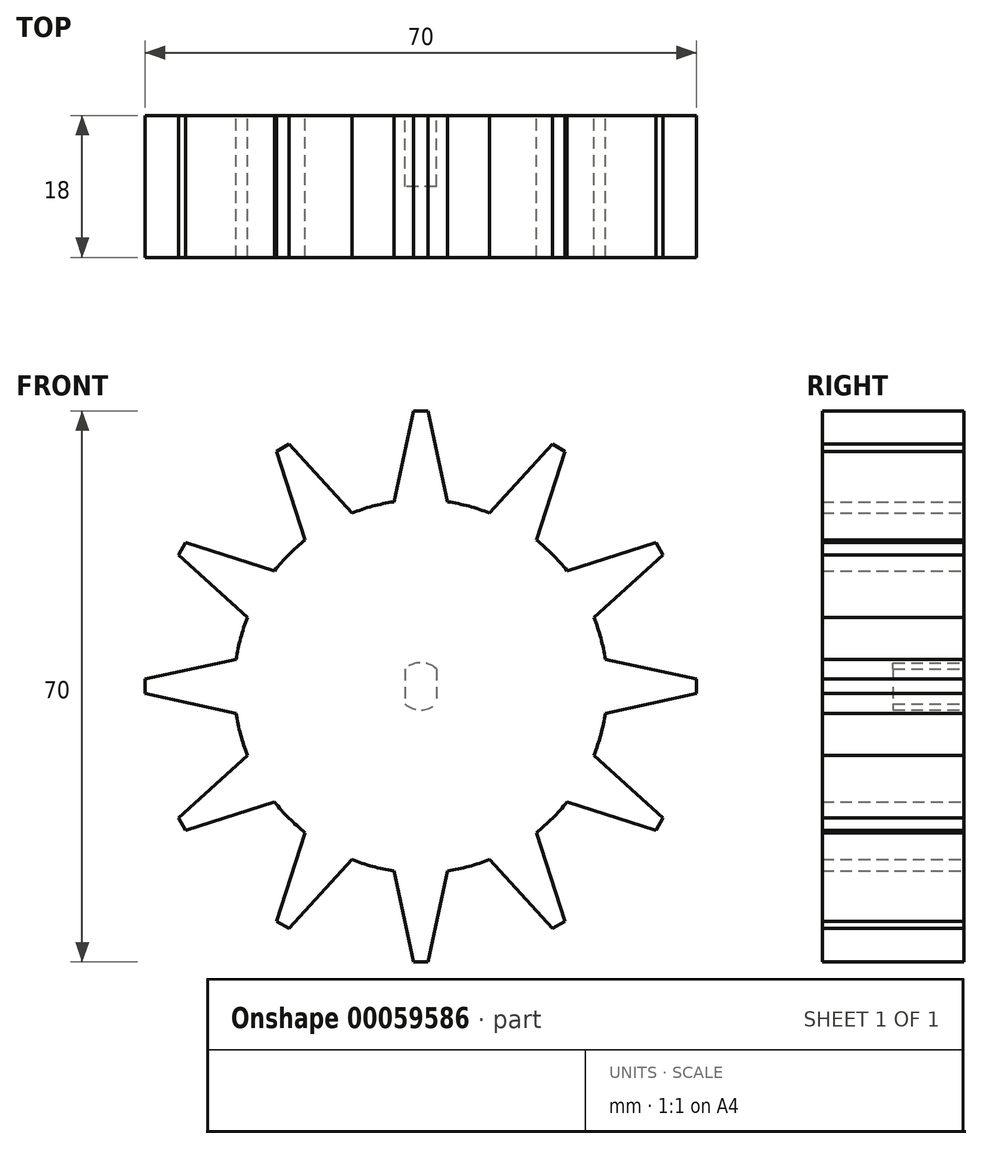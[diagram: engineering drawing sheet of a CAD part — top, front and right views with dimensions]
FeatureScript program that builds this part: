
annotation { "Feature Type Name" : "Feature", "Feature Type Description" : "" }
export const myFeature = defineFeature(function(context is Context, id is Id, definition is map)
    precondition{}
    {
        {
            var Q0;
            Q0=qCreatedBy(makeId("Front.planeOp"),FACE);
            var sketch = newSketch(context, id + "F0", { "sketchPlane" : qUnion([Q0])});
            skLineSegment(sketch, "E0", {"start": v(0, 0) * mm, "end": v(0, 35) * mm, "construction": true});
            skLineSegment(sketch, "E1", {"start": v(-0.91, 35) * mm, "end": v(0.91, 35) * mm, "construction": true});
            skLineSegment(sketch, "E2", {"start": v(0, 35) * mm, "end": v(0, 23.75) * mm, "construction": true});
            skPoint(sketch, "E3.startSnap0", {"position": v(0, 31.5) * mm});
            skLineSegment(sketch, "E4", {"start": v(-0.91, 35) * mm, "end": v(0, 35) * mm});
            skLineSegment(sketch, "E5.MirrorCS", {"start": v(0.91, 35) * mm, "end": v(0, 35) * mm});
            skLineSegment(sketch, "E6.MirrorCS", {"start": v(0.91, 35) * mm, "end": v(-0.91, 35) * mm, "construction": true});
            skCircle(sketch, "E7", {"center": v(0, 0) * mm, "radius": 23.69 * mm});
            skLineSegment(sketch, "E8", {"start": v(0.92, 35) * mm, "end": v(3.42, 23.44) * mm});
            skLineSegment(sketch, "E9", {"start": v(-0.91, 35) * mm, "end": v(-3.42, 23.44) * mm});
            skPoint(sketch, "E10.1.0", {"position": v(-15.75, 27.28) * mm});
            skLineSegment(sketch, "E10.1.1", {"start": v(-16.7, 30.77) * mm, "end": v(-8.76, 22) * mm});
            skLineSegment(sketch, "E10.1.2", {"start": v(-17.5, 30.31) * mm, "end": v(-11.87, 20.57) * mm, "construction": true});
            skLineSegment(sketch, "E10.1.3", {"start": v(-18.3, 29.85) * mm, "end": v(-14.68, 18.59) * mm});
            skPoint(sketch, "E10.1.4", {"position": v(-15.75, 27.28) * mm});
            skLineSegment(sketch, "E10.1.5", {"start": v(-16.7, 30.77) * mm, "end": v(-18.3, 29.85) * mm, "construction": true});
            skLineSegment(sketch, "E10.1.6", {"start": v(-18.3, 29.85) * mm, "end": v(-16.7, 30.77) * mm, "construction": true});
            skLineSegment(sketch, "E10.1.7", {"start": v(-16.7, 30.77) * mm, "end": v(-17.5, 30.31) * mm});
            skLineSegment(sketch, "E10.1.8", {"start": v(-18.3, 29.85) * mm, "end": v(-17.5, 30.31) * mm});
            skPoint(sketch, "E10.2.0", {"position": v(-27.28, 15.75) * mm});
            skLineSegment(sketch, "E10.2.1", {"start": v(-29.85, 18.3) * mm, "end": v(-18.59, 14.68) * mm});
            skLineSegment(sketch, "E10.2.2", {"start": v(-30.31, 17.5) * mm, "end": v(-20.57, 11.88) * mm, "construction": true});
            skLineSegment(sketch, "E10.2.3", {"start": v(-30.77, 16.7) * mm, "end": v(-22, 8.76) * mm});
            skPoint(sketch, "E10.2.4", {"position": v(-27.28, 15.75) * mm});
            skLineSegment(sketch, "E10.2.5", {"start": v(-29.85, 18.3) * mm, "end": v(-30.77, 16.7) * mm, "construction": true});
            skLineSegment(sketch, "E10.2.6", {"start": v(-30.77, 16.7) * mm, "end": v(-29.85, 18.3) * mm, "construction": true});
            skLineSegment(sketch, "E10.2.7", {"start": v(-29.85, 18.3) * mm, "end": v(-30.31, 17.5) * mm});
            skLineSegment(sketch, "E10.2.8", {"start": v(-30.77, 16.7) * mm, "end": v(-30.31, 17.5) * mm});
            skPoint(sketch, "E10.3.0", {"position": v(-31.5, 0) * mm});
            skLineSegment(sketch, "E10.3.1", {"start": v(-35, 0.92) * mm, "end": v(-23.44, 3.42) * mm});
            skLineSegment(sketch, "E10.3.2", {"start": v(-35, 0) * mm, "end": v(-23.75, 0) * mm, "construction": true});
            skLineSegment(sketch, "E10.3.3", {"start": v(-35, -0.91) * mm, "end": v(-23.44, -3.42) * mm});
            skPoint(sketch, "E10.3.4", {"position": v(-31.5, 0) * mm});
            skLineSegment(sketch, "E10.3.5", {"start": v(-35, 0.92) * mm, "end": v(-35, -0.91) * mm, "construction": true});
            skLineSegment(sketch, "E10.3.6", {"start": v(-35, -0.91) * mm, "end": v(-35, 0.92) * mm, "construction": true});
            skLineSegment(sketch, "E10.3.7", {"start": v(-35, 0.92) * mm, "end": v(-35, 0) * mm});
            skLineSegment(sketch, "E10.3.8", {"start": v(-35, -0.91) * mm, "end": v(-35, 0) * mm});
            skPoint(sketch, "E10.4.0", {"position": v(-27.28, -15.75) * mm});
            skLineSegment(sketch, "E10.4.1", {"start": v(-30.77, -16.7) * mm, "end": v(-22, -8.76) * mm});
            skLineSegment(sketch, "E10.4.2", {"start": v(-30.31, -17.5) * mm, "end": v(-20.57, -11.87) * mm, "construction": true});
            skLineSegment(sketch, "E10.4.3", {"start": v(-29.85, -18.3) * mm, "end": v(-18.59, -14.68) * mm});
            skPoint(sketch, "E10.4.4", {"position": v(-27.28, -15.75) * mm});
            skLineSegment(sketch, "E10.4.5", {"start": v(-30.77, -16.7) * mm, "end": v(-29.85, -18.3) * mm, "construction": true});
            skLineSegment(sketch, "E10.4.6", {"start": v(-29.85, -18.3) * mm, "end": v(-30.77, -16.7) * mm, "construction": true});
            skLineSegment(sketch, "E10.4.7", {"start": v(-30.77, -16.7) * mm, "end": v(-30.31, -17.5) * mm});
            skLineSegment(sketch, "E10.4.8", {"start": v(-29.85, -18.3) * mm, "end": v(-30.31, -17.5) * mm});
            skPoint(sketch, "E10.5.0", {"position": v(-15.75, -27.28) * mm});
            skLineSegment(sketch, "E10.5.1", {"start": v(-18.3, -29.85) * mm, "end": v(-14.68, -18.59) * mm});
            skLineSegment(sketch, "E10.5.2", {"start": v(-17.5, -30.31) * mm, "end": v(-11.87, -20.57) * mm, "construction": true});
            skLineSegment(sketch, "E10.5.3", {"start": v(-16.7, -30.77) * mm, "end": v(-8.76, -22) * mm});
            skPoint(sketch, "E10.5.4", {"position": v(-15.75, -27.28) * mm});
            skLineSegment(sketch, "E10.5.5", {"start": v(-18.3, -29.85) * mm, "end": v(-16.7, -30.77) * mm, "construction": true});
            skLineSegment(sketch, "E10.5.6", {"start": v(-16.7, -30.77) * mm, "end": v(-18.3, -29.85) * mm, "construction": true});
            skLineSegment(sketch, "E10.5.7", {"start": v(-18.3, -29.85) * mm, "end": v(-17.5, -30.31) * mm});
            skLineSegment(sketch, "E10.5.8", {"start": v(-16.7, -30.77) * mm, "end": v(-17.5, -30.31) * mm});
            skPoint(sketch, "E10.6.0", {"position": v(0, -31.5) * mm});
            skLineSegment(sketch, "E10.6.1", {"start": v(-0.92, -35) * mm, "end": v(-3.42, -23.44) * mm});
            skLineSegment(sketch, "E10.6.2", {"start": v(0, -35) * mm, "end": v(0, -23.75) * mm, "construction": true});
            skLineSegment(sketch, "E10.6.3", {"start": v(0.91, -35) * mm, "end": v(3.42, -23.44) * mm});
            skPoint(sketch, "E10.6.4", {"position": v(0, -31.5) * mm});
            skLineSegment(sketch, "E10.6.5", {"start": v(-0.92, -35) * mm, "end": v(0.91, -35) * mm, "construction": true});
            skLineSegment(sketch, "E10.6.6", {"start": v(0.91, -35) * mm, "end": v(-0.92, -35) * mm, "construction": true});
            skLineSegment(sketch, "E10.6.7", {"start": v(-0.92, -35) * mm, "end": v(0, -35) * mm});
            skLineSegment(sketch, "E10.6.8", {"start": v(0.91, -35) * mm, "end": v(0, -35) * mm});
            skPoint(sketch, "E10.7.0", {"position": v(15.75, -27.28) * mm});
            skLineSegment(sketch, "E10.7.1", {"start": v(16.7, -30.77) * mm, "end": v(8.76, -22) * mm});
            skLineSegment(sketch, "E10.7.2", {"start": v(17.5, -30.31) * mm, "end": v(11.87, -20.57) * mm, "construction": true});
            skLineSegment(sketch, "E10.7.3", {"start": v(18.3, -29.85) * mm, "end": v(14.68, -18.59) * mm});
            skPoint(sketch, "E10.7.4", {"position": v(15.75, -27.28) * mm});
            skLineSegment(sketch, "E10.7.5", {"start": v(16.7, -30.77) * mm, "end": v(18.3, -29.85) * mm, "construction": true});
            skLineSegment(sketch, "E10.7.6", {"start": v(18.3, -29.85) * mm, "end": v(16.7, -30.77) * mm, "construction": true});
            skLineSegment(sketch, "E10.7.7", {"start": v(16.7, -30.77) * mm, "end": v(17.5, -30.31) * mm});
            skLineSegment(sketch, "E10.7.8", {"start": v(18.3, -29.85) * mm, "end": v(17.5, -30.31) * mm});
            skPoint(sketch, "E10.8.0", {"position": v(27.28, -15.75) * mm});
            skLineSegment(sketch, "E10.8.1", {"start": v(29.85, -18.3) * mm, "end": v(18.59, -14.68) * mm});
            skLineSegment(sketch, "E10.8.2", {"start": v(30.31, -17.5) * mm, "end": v(20.57, -11.88) * mm, "construction": true});
            skLineSegment(sketch, "E10.8.3", {"start": v(30.77, -16.7) * mm, "end": v(22, -8.76) * mm});
            skPoint(sketch, "E10.8.4", {"position": v(27.28, -15.75) * mm});
            skLineSegment(sketch, "E10.8.5", {"start": v(29.85, -18.3) * mm, "end": v(30.77, -16.7) * mm, "construction": true});
            skLineSegment(sketch, "E10.8.6", {"start": v(30.77, -16.7) * mm, "end": v(29.85, -18.3) * mm, "construction": true});
            skLineSegment(sketch, "E10.8.7", {"start": v(29.85, -18.3) * mm, "end": v(30.31, -17.5) * mm});
            skLineSegment(sketch, "E10.8.8", {"start": v(30.77, -16.7) * mm, "end": v(30.31, -17.5) * mm});
            skPoint(sketch, "E10.9.0", {"position": v(31.5, 0) * mm});
            skLineSegment(sketch, "E10.9.1", {"start": v(35, -0.92) * mm, "end": v(23.44, -3.42) * mm});
            skLineSegment(sketch, "E10.9.2", {"start": v(35, 0) * mm, "end": v(23.75, 0) * mm, "construction": true});
            skLineSegment(sketch, "E10.9.3", {"start": v(35, 0.91) * mm, "end": v(23.44, 3.42) * mm});
            skPoint(sketch, "E10.9.4", {"position": v(31.5, 0) * mm});
            skLineSegment(sketch, "E10.9.5", {"start": v(35, -0.92) * mm, "end": v(35, 0.91) * mm, "construction": true});
            skLineSegment(sketch, "E10.9.6", {"start": v(35, 0.91) * mm, "end": v(35, -0.92) * mm, "construction": true});
            skLineSegment(sketch, "E10.9.7", {"start": v(35, -0.92) * mm, "end": v(35, 0) * mm});
            skLineSegment(sketch, "E10.9.8", {"start": v(35, 0.91) * mm, "end": v(35, 0) * mm});
            skPoint(sketch, "E10.10.0", {"position": v(27.28, 15.75) * mm});
            skLineSegment(sketch, "E10.10.1", {"start": v(30.77, 16.7) * mm, "end": v(22, 8.76) * mm});
            skLineSegment(sketch, "E10.10.2", {"start": v(30.31, 17.5) * mm, "end": v(20.57, 11.88) * mm, "construction": true});
            skLineSegment(sketch, "E10.10.3", {"start": v(29.85, 18.3) * mm, "end": v(18.59, 14.68) * mm});
            skPoint(sketch, "E10.10.4", {"position": v(27.28, 15.75) * mm});
            skLineSegment(sketch, "E10.10.5", {"start": v(30.77, 16.7) * mm, "end": v(29.85, 18.3) * mm, "construction": true});
            skLineSegment(sketch, "E10.10.6", {"start": v(29.85, 18.3) * mm, "end": v(30.77, 16.7) * mm, "construction": true});
            skLineSegment(sketch, "E10.10.7", {"start": v(30.77, 16.7) * mm, "end": v(30.31, 17.5) * mm});
            skLineSegment(sketch, "E10.10.8", {"start": v(29.85, 18.3) * mm, "end": v(30.31, 17.5) * mm});
            skPoint(sketch, "E10.11.0", {"position": v(15.75, 27.28) * mm});
            skLineSegment(sketch, "E10.11.1", {"start": v(18.3, 29.85) * mm, "end": v(14.68, 18.59) * mm});
            skLineSegment(sketch, "E10.11.2", {"start": v(17.5, 30.31) * mm, "end": v(11.88, 20.57) * mm, "construction": true});
            skLineSegment(sketch, "E10.11.3", {"start": v(16.7, 30.77) * mm, "end": v(8.76, 22) * mm});
            skPoint(sketch, "E10.11.4", {"position": v(15.75, 27.28) * mm});
            skLineSegment(sketch, "E10.11.5", {"start": v(18.3, 29.85) * mm, "end": v(16.7, 30.77) * mm, "construction": true});
            skLineSegment(sketch, "E10.11.6", {"start": v(16.7, 30.77) * mm, "end": v(18.3, 29.85) * mm, "construction": true});
            skLineSegment(sketch, "E10.11.7", {"start": v(18.3, 29.85) * mm, "end": v(17.5, 30.31) * mm});
            skLineSegment(sketch, "E10.11.8", {"start": v(16.7, 30.77) * mm, "end": v(17.5, 30.31) * mm});
            skSolve(sketch);
        }
        {
            var Q0;
            Q0 = qSketchRegion(id + "F0", true);
            extrude(context, id + "F1", {"entities" : qUnion([Q0]), "depth" : 18 * mm});
        }
        {
            var Q0;
            Q0=makeQuery(id+"F1.opExtrude","CAP_FACE",FACE,{"disambiguationData":[OSD([sQuery(id+"F0.wireOp",EDGE,"E4"),sQuery(id+"F0.wireOp",EDGE,"E5.MirrorCS"),sQuery(id+"F0.wireOp",EDGE,"E7"),sQuery(id+"F0.wireOp",EDGE,"E8"),sQuery(id+"F0.wireOp",EDGE,"E9"),sQuery(id+"F0.wireOp",EDGE,"E10.1.1"),sQuery(id+"F0.wireOp",EDGE,"E10.1.3"),sQuery(id+"F0.wireOp",EDGE,"E10.1.7"),sQuery(id+"F0.wireOp",EDGE,"E10.1.8"),sQuery(id+"F0.wireOp",EDGE,"E10.2.1"),sQuery(id+"F0.wireOp",EDGE,"E10.2.3"),sQuery(id+"F0.wireOp",EDGE,"E10.2.7"),sQuery(id+"F0.wireOp",EDGE,"E10.2.8"),sQuery(id+"F0.wireOp",EDGE,"E10.3.1"),sQuery(id+"F0.wireOp",EDGE,"E10.3.3"),sQuery(id+"F0.wireOp",EDGE,"E10.3.7"),sQuery(id+"F0.wireOp",EDGE,"E10.3.8"),sQuery(id+"F0.wireOp",EDGE,"E10.4.1"),sQuery(id+"F0.wireOp",EDGE,"E10.4.3"),sQuery(id+"F0.wireOp",EDGE,"E10.4.7"),sQuery(id+"F0.wireOp",EDGE,"E10.4.8"),sQuery(id+"F0.wireOp",EDGE,"E10.5.1"),sQuery(id+"F0.wireOp",EDGE,"E10.5.3"),sQuery(id+"F0.wireOp",EDGE,"E10.5.7"),sQuery(id+"F0.wireOp",EDGE,"E10.5.8"),sQuery(id+"F0.wireOp",EDGE,"E10.6.1"),sQuery(id+"F0.wireOp",EDGE,"E10.6.3"),sQuery(id+"F0.wireOp",EDGE,"E10.6.7"),sQuery(id+"F0.wireOp",EDGE,"E10.6.8"),sQuery(id+"F0.wireOp",EDGE,"E10.7.1"),sQuery(id+"F0.wireOp",EDGE,"E10.7.3"),sQuery(id+"F0.wireOp",EDGE,"E10.7.7"),sQuery(id+"F0.wireOp",EDGE,"E10.7.8"),sQuery(id+"F0.wireOp",EDGE,"E10.8.1"),sQuery(id+"F0.wireOp",EDGE,"E10.8.3"),sQuery(id+"F0.wireOp",EDGE,"E10.8.7"),sQuery(id+"F0.wireOp",EDGE,"E10.8.8"),sQuery(id+"F0.wireOp",EDGE,"E10.9.1"),sQuery(id+"F0.wireOp",EDGE,"E10.9.3"),sQuery(id+"F0.wireOp",EDGE,"E10.9.7"),sQuery(id+"F0.wireOp",EDGE,"E10.9.8"),sQuery(id+"F0.wireOp",EDGE,"E10.10.1"),sQuery(id+"F0.wireOp",EDGE,"E10.10.3"),sQuery(id+"F0.wireOp",EDGE,"E10.10.7"),sQuery(id+"F0.wireOp",EDGE,"E10.10.8"),sQuery(id+"F0.wireOp",EDGE,"E10.11.1"),sQuery(id+"F0.wireOp",EDGE,"E10.11.3"),sQuery(id+"F0.wireOp",EDGE,"E10.11.7"),sQuery(id+"F0.wireOp",EDGE,"E10.11.8")])],"isStart":true});
            var sketch = newSketch(context, id + "F2", { "sketchPlane" : qUnion([Q0])});
            skArc(sketch, "E11", {"start": v(-2, -2.24) * mm, "mid": v(0, -3) * mm, "end": v(2, -2.24) * mm});
            skLineSegment(sketch, "E12.left", {"start": v(-2, 2.24) * mm, "end": v(-2, -2.24) * mm});
            skLineSegment(sketch, "E12.right", {"start": v(2, 2.24) * mm, "end": v(2, -2.24) * mm});
            skPoint(sketch, "E13.orphan", {"position": v(-2, 2.5) * mm});
            skPoint(sketch, "E14.trimOffspring.end.orphan", {"position": v(2, 2.5) * mm});
            skPoint(sketch, "E15.orphan", {"position": v(-2, -2.5) * mm});
            skPoint(sketch, "E16.orphan", {"position": v(2, -2.5) * mm});
            skArc(sketch, "E17.trimOffspring", {"start": v(2, 2.24) * mm, "mid": v(0, 3) * mm, "end": v(-2, 2.24) * mm});
            skSolve(sketch);
        }
        {
            var Q0;
            Q0 = qSketchRegion(id + "F2", true);
            extrude(context, id + "F3", {"entities" : qUnion([Q0]), "operationType" : NewBodyOperationType.REMOVE, "oppositeDirection" : true, "depth" : 9 * mm, "offsetDistance" : 25 * mm});
        }
    });
